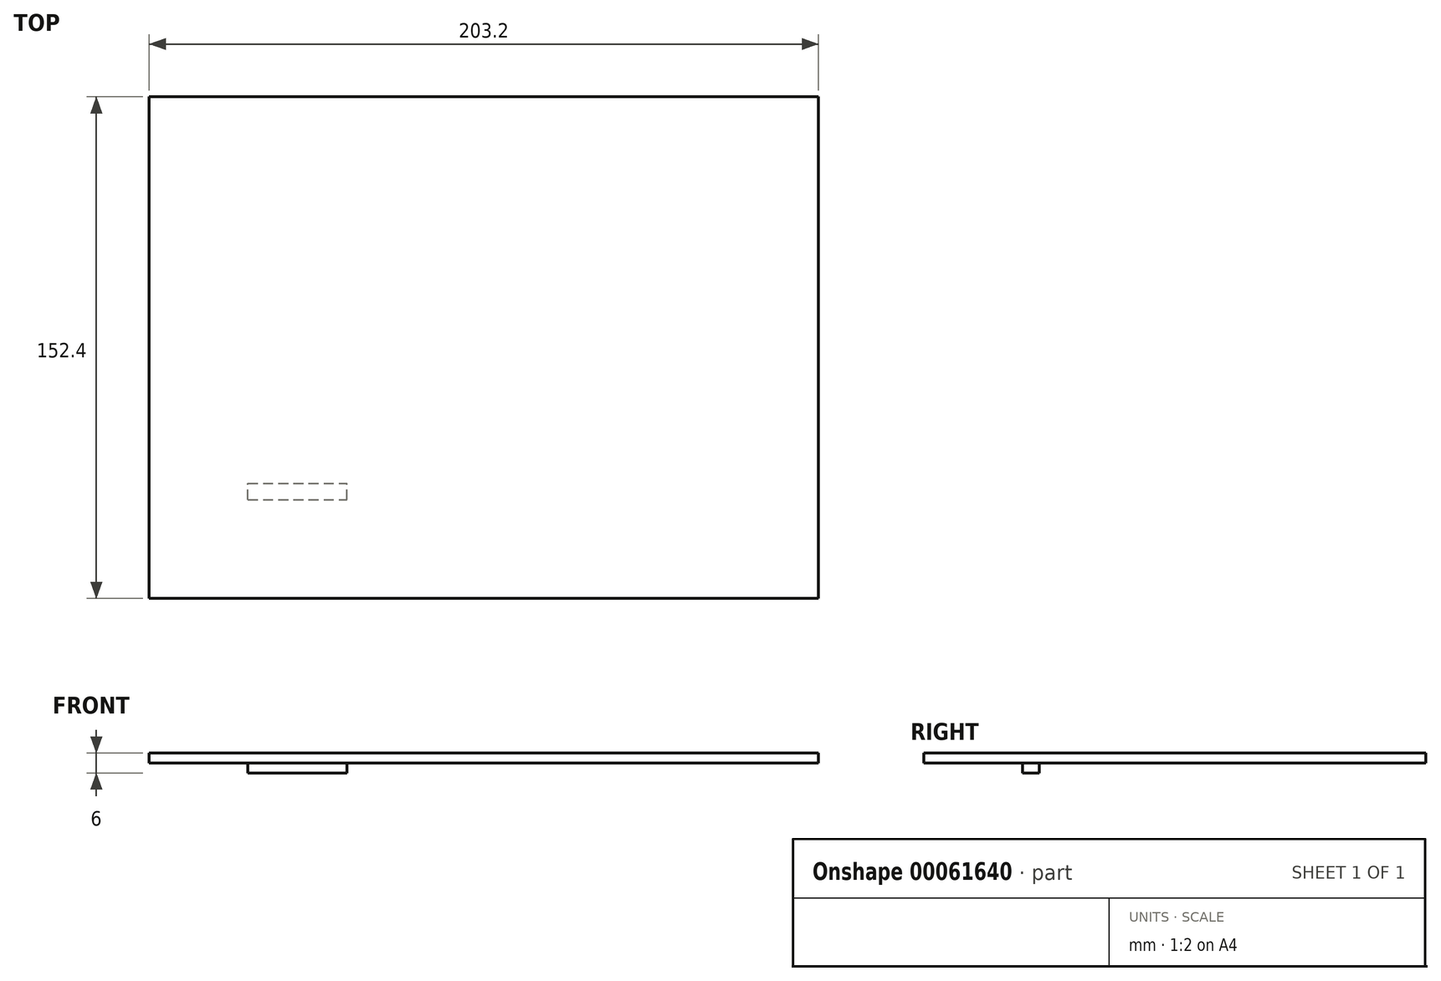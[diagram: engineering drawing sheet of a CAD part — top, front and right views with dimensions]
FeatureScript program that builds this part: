
annotation { "Feature Type Name" : "Feature", "Feature Type Description" : "" }
export const myFeature = defineFeature(function(context is Context, id is Id, definition is map)
    precondition{}
    {
        {
            var Q0;
            Q0=qCreatedBy(makeId("Top.planeOp"),FACE);
            var sketch = newSketch(context, id + "F0", { "sketchPlane" : qUnion([Q0])});
            skLineSegment(sketch, "E0.bottom", {"start": v(-64.95, 117.12) * mm, "end": v(138.25, 117.12) * mm});
            skLineSegment(sketch, "E0.top", {"start": v(-64.95, -35.28) * mm, "end": v(138.25, -35.28) * mm});
            skLineSegment(sketch, "E0.left", {"start": v(-64.95, 117.12) * mm, "end": v(-64.95, -35.28) * mm});
            skLineSegment(sketch, "E0.right", {"start": v(138.25, 117.12) * mm, "end": v(138.25, -35.28) * mm});
            skSolve(sketch);
        }
        {
            var Q0;
            Q0=makeQuery(id+"F0.imprint","IMPRINT",FACE,{"disambiguationData":[TD([[makeQuery(id+"F0.imprint","IMPRINT",EDGE,{"derivedFrom":sQuery(id+"F0.wireOp",EDGE,"E0.bottom")}),-1.0]])]});
            extrude(context, id + "F1", {"entities" : qUnion([Q0]), "depth" : 3 * mm});
        }
        {
            var Q0;
            Q0=makeQuery(id+"F1.opExtrude","CAP_FACE",FACE,{"disambiguationData":[OSD([sQuery(id+"F0.wireOp",EDGE,"E0.bottom"),sQuery(id+"F0.wireOp",EDGE,"E0.top"),sQuery(id+"F0.wireOp",EDGE,"E0.left"),sQuery(id+"F0.wireOp",EDGE,"E0.right")])],"isStart":true});
            var sketch = newSketch(context, id + "F2", { "sketchPlane" : qUnion([Q0])});
            skLineSegment(sketch, "E1.bottom", {"start": v(-34.95, 5.28) * mm, "end": v(-4.95, 5.28) * mm});
            skLineSegment(sketch, "E1.top", {"start": v(-34.95, 0.28) * mm, "end": v(-4.95, 0.28) * mm});
            skLineSegment(sketch, "E1.left", {"start": v(-34.95, 5.28) * mm, "end": v(-34.95, 0.28) * mm});
            skLineSegment(sketch, "E1.right", {"start": v(-4.95, 5.28) * mm, "end": v(-4.95, 0.28) * mm});
            skSolve(sketch);
        }
        {
            var Q0;
            Q0=makeQuery(id+"F2.imprint","IMPRINT",FACE,{"disambiguationData":[TD([[makeQuery(id+"F2.imprint","IMPRINT",EDGE,{"derivedFrom":sQuery(id+"F2.wireOp",EDGE,"E1.bottom")}),-1.0]])]});
            extrude(context, id + "F3", {"entities" : qUnion([Q0]), "operationType" : NewBodyOperationType.ADD, "depth" : 3 * mm});
        }
    });
